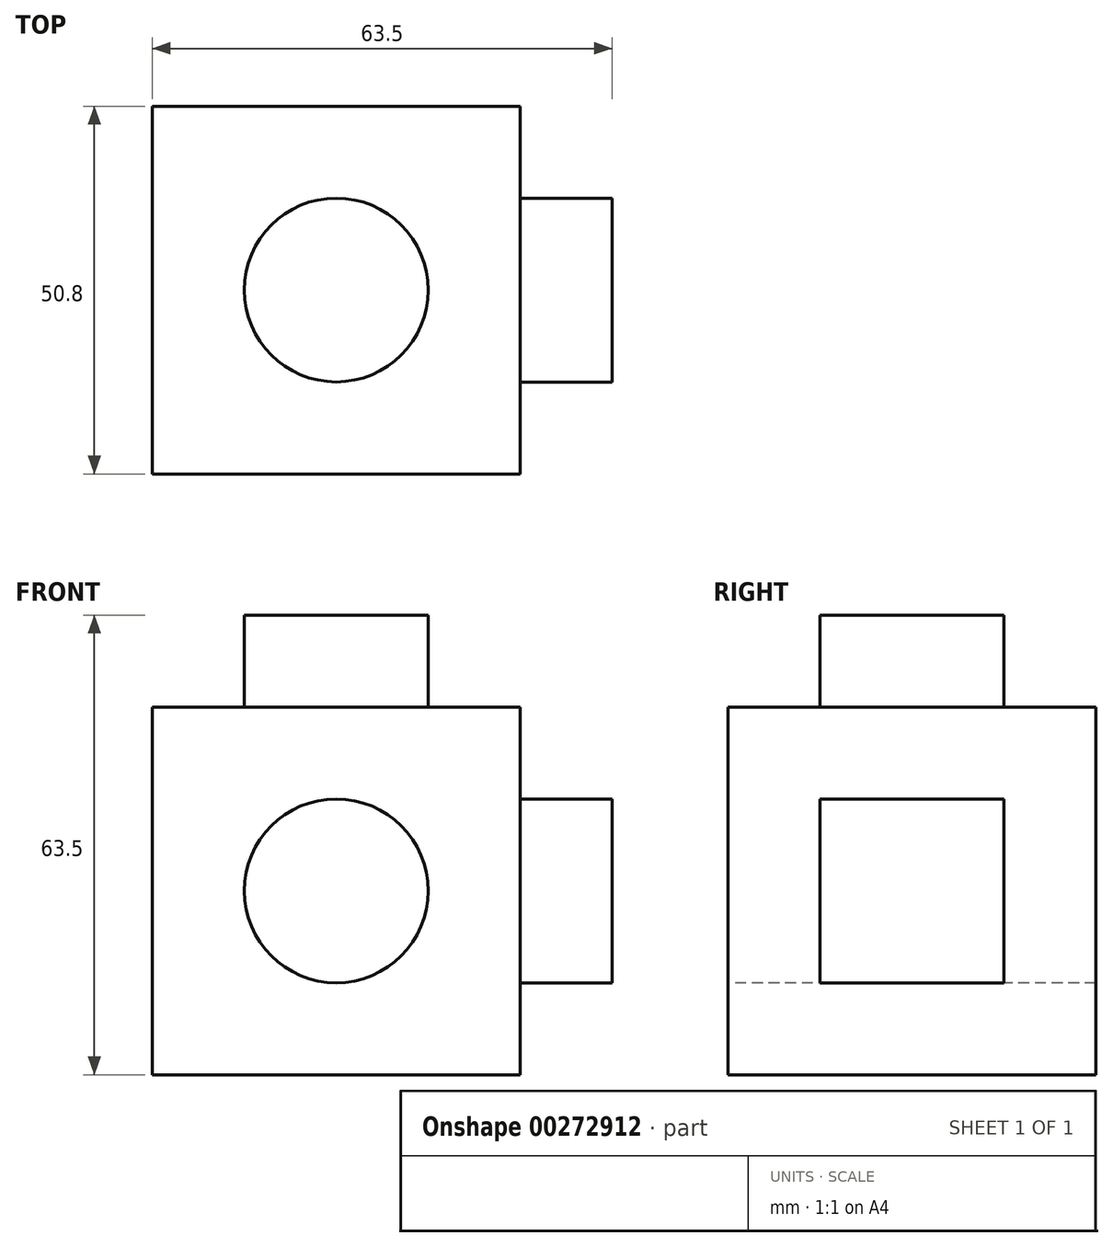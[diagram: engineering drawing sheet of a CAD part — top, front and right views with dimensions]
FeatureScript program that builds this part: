
annotation { "Feature Type Name" : "Feature", "Feature Type Description" : "" }
export const myFeature = defineFeature(function(context is Context, id is Id, definition is map)
    precondition{}
    {
        {
            var Q0;
            Q0=qCreatedBy(makeId("Front.planeOp"),FACE);
            var sketch = newSketch(context, id + "F0", { "sketchPlane" : qUnion([Q0])});
            skLineSegment(sketch, "E0.bottom", {"start": v(0, 0) * mm, "end": v(-50.8, 0) * mm});
            skLineSegment(sketch, "E0.top", {"start": v(0, 50.8) * mm, "end": v(-50.8, 50.8) * mm});
            skLineSegment(sketch, "E0.left", {"start": v(0, 0) * mm, "end": v(0, 50.8) * mm});
            skLineSegment(sketch, "E0.right", {"start": v(-50.8, 0) * mm, "end": v(-50.8, 50.8) * mm});
            skSolve(sketch);
        }
        {
            var Q0;
            Q0 = qSketchRegion(id + "F0", true);
            extrude(context, id + "F1", {"entities" : qUnion([Q0]), "depth" : 50.8 * mm});
        }
        {
            var Q0;
            Q0=makeQuery(id+"F1.opExtrude","CAP_FACE",FACE,{"disambiguationData":[OSD([sQuery(id+"F0.wireOp",EDGE,"E0.bottom"),sQuery(id+"F0.wireOp",EDGE,"E0.top"),sQuery(id+"F0.wireOp",EDGE,"E0.left"),sQuery(id+"F0.wireOp",EDGE,"E0.right")])],"isStart":false});
            var sketch = newSketch(context, id + "F2", { "sketchPlane" : qUnion([Q0])});
            skCircle(sketch, "E1", {"center": v(-25.4, 25.4) * mm, "radius": 12.7 * mm});
            skSolve(sketch);
        }
        {
            var Q0;
            Q0=makeQuery(id+"F2.imprint","IMPRINT",FACE,{"disambiguationData":[TD([[makeQuery(id+"F2.imprint","IMPRINT",EDGE,{"derivedFrom":sQuery(id+"F2.wireOp",EDGE,"E1")}),1.0]])]});
            extrude(context, id + "F3", {"entities" : qUnion([Q0]), "operationType" : NewBodyOperationType.REMOVE, "oppositeDirection" : true, "depth" : 50.8 * mm});
        }
        {
            var Q0;
            Q0=makeQuery(id+"F1.opExtrude","SWEPT_FACE",FACE,{"disambiguationData":[OSD([sQuery(id+"F0.wireOp",EDGE,"E0.right")])]});
            var sketch = newSketch(context, id + "F4", { "sketchPlane" : qUnion([Q0])});
            skCircle(sketch, "E2", {"center": v(25.4, 25.4) * mm, "radius": 12.7 * mm});
            skSolve(sketch);
        }
        {
            var Q0;
            Q0=makeQuery(id+"F1.opExtrude","SWEPT_FACE",FACE,{"disambiguationData":[OSD([sQuery(id+"F0.wireOp",EDGE,"E0.top")])]});
            var sketch = newSketch(context, id + "F5", { "sketchPlane" : qUnion([Q0])});
            skCircle(sketch, "E3", {"center": v(-25.4, -25.4) * mm, "radius": 12.7 * mm});
            skSolve(sketch);
        }
        {
            var Q0;
            Q0=makeQuery(id+"F5.imprint","IMPRINT",FACE,{"disambiguationData":[TD([[makeQuery(id+"F5.imprint","IMPRINT",EDGE,{"derivedFrom":sQuery(id+"F5.wireOp",EDGE,"E3")}),1.0]])]});
            extrude(context, id + "F6", {"entities" : qUnion([Q0]), "operationType" : NewBodyOperationType.ADD, "depth" : 12.7 * mm});
        }
        {
            var Q0;
            Q0=makeQuery(id+"F1.opExtrude","SWEPT_FACE",FACE,{"disambiguationData":[OSD([sQuery(id+"F0.wireOp",EDGE,"E0.left")])]});
            var sketch = newSketch(context, id + "F7", { "sketchPlane" : qUnion([Q0])});
            skLineSegment(sketch, "E4.bottom", {"start": v(-12.7, 12.7) * mm, "end": v(-38.1, 12.7) * mm});
            skLineSegment(sketch, "E4.top", {"start": v(-12.7, 38.1) * mm, "end": v(-38.1, 38.1) * mm});
            skLineSegment(sketch, "E4.left", {"start": v(-12.7, 12.7) * mm, "end": v(-12.7, 38.1) * mm});
            skLineSegment(sketch, "E4.right", {"start": v(-38.1, 12.7) * mm, "end": v(-38.1, 38.1) * mm});
            skSolve(sketch);
        }
        {
            var Q0;
            Q0=makeQuery(id+"F7.imprint","IMPRINT",FACE,{"disambiguationData":[TD([[makeQuery(id+"F7.imprint","IMPRINT",EDGE,{"derivedFrom":sQuery(id+"F7.wireOp",EDGE,"E4.bottom")}),-1.0]])]});
            extrude(context, id + "F8", {"entities" : qUnion([Q0]), "operationType" : NewBodyOperationType.ADD, "depth" : 12.7 * mm});
        }
    });
